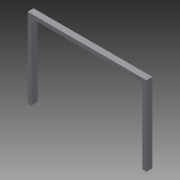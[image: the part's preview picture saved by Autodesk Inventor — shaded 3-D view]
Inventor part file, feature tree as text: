
AUTODESK INVENTOR PART (.ipt)
format: ipt  version: 2015 (Build 190159000, 159)  size: 86,528 bytes
history: native  units: mm
features: extrude x1, fillet x1, sketch x1
ambient origin geometry x8: Origin, YZ Plane, XZ Plane, XY Plane, X Axis, Y Axis, Z Axis, Center Point
bodies: Solid1 (feature_tree)
feature tree (3):
  extrude  "Extrusion1"  TaperAngle=0.0deg  [1 undecoded]
  fillet  "Fillet1"  Radius=2.0mm
  sketch  "Sketch1"  dims[d0=2.0mm d1=0.0mm d2=2.0mm d3=2.0mm d4=60.0mm d5=40.0mm d6=40.0mm d7=3.0mm d8=0.0mm d9=2.0mm]
note: 1 required parameter value undecoded (feature->parameter linkage not recoverable at this tier; creation-order binding heuristic only, values carry confidence <= 0.55)
